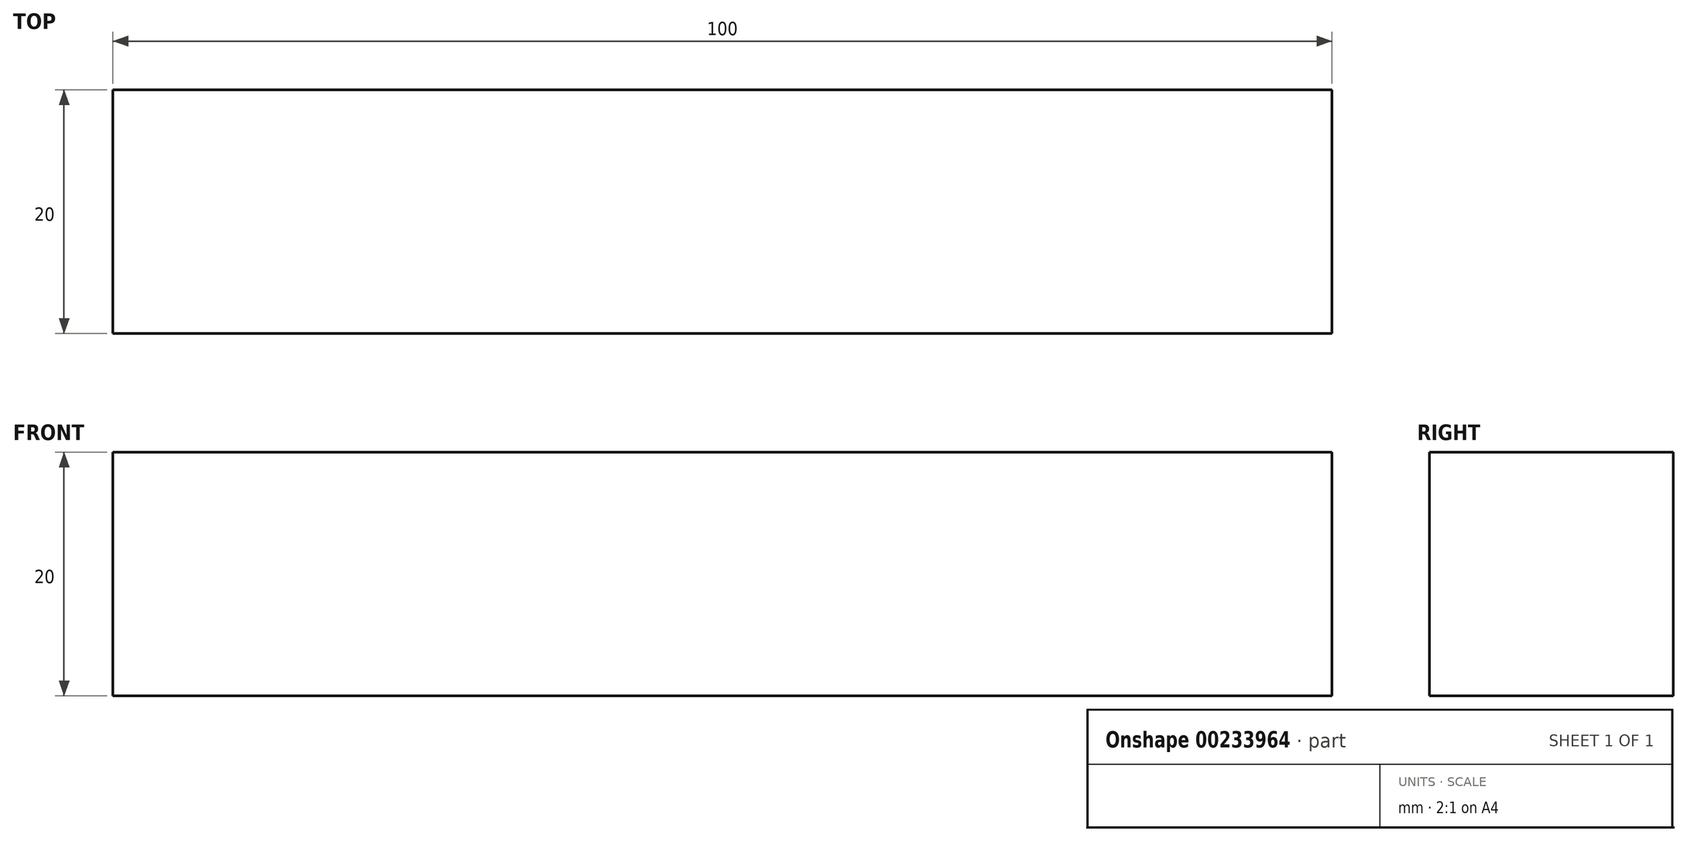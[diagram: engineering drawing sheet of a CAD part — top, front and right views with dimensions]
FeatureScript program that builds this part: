
annotation { "Feature Type Name" : "Feature", "Feature Type Description" : "" }
export const myFeature = defineFeature(function(context is Context, id is Id, definition is map)
    precondition{}
    {
        {
            var Q0;
            Q0=qCreatedBy(makeId("Right.planeOp"),FACE);
            var sketch = newSketch(context, id + "F0", { "sketchPlane" : qUnion([Q0])});
            skLineSegment(sketch, "E0.bottom", {"start": v(10, 10) * mm, "end": v(-10, 10) * mm});
            skLineSegment(sketch, "E0.top", {"start": v(10, -10) * mm, "end": v(-10, -10) * mm});
            skLineSegment(sketch, "E0.left", {"start": v(10, 10) * mm, "end": v(10, -10) * mm});
            skLineSegment(sketch, "E0.right", {"start": v(-10, 10) * mm, "end": v(-10, -10) * mm});
            skPoint(sketch, "E0.middle", {"position": v(0, 0) * mm});
            skSolve(sketch);
        }
        {
            var Q0;
            Q0=makeQuery(id+"F0.imprint","IMPRINT",FACE,{"disambiguationData":[TD([[makeQuery(id+"F0.imprint","IMPRINT",EDGE,{"derivedFrom":sQuery(id+"F0.wireOp",EDGE,"E0.bottom")}),1.0]])]});
            extrude(context, id + "F1", {"entities" : qUnion([Q0]), "endBound" : BoundingType.SYMMETRIC, "depth" : 100 * mm});
        }
    });
